# Revit family: VENTS VUTR 281-401 V EC
name_source: partatom
category: Mechanical Equipment
units: mm (PartAtom-declared; Revit-internal decimal feet)

## family parameters
Always vertical = Yes
Cut with Voids When Loaded = No
OmniClass Number = 23.75.00.00
OmniClass Title = Climate Control (HVAC)
Part Type = Normal
Room Calculation Point = No
Round Connector Dimension = Use Diameter
Shared = No
Work Plane-Based = No

## types (8) — shared parameters
00_20_Manufacturer = Vents
00_20_Name = Single-room air handling unit with heat recovery
Casing Material = Polymer-coated steel (white)
D = 160 mm  [stored 0.524934 ft]
Filter = G4
Frequency = 60 Hz
H = 588 mm  [stored 1.92913 ft]
H1 = 638 mm  [stored 2.09318 ft]
L = 515 mm  [stored 1.68963 ft]
L1 = 209 mm  [stored 0.685696 ft]
Load Classification = HVAC
Maintenance zone material = <By Category>
Number of Fase = 1
Voltage = 230 V
W = 598 mm  [stored 1.96194 ft]
W1 = 397 mm  [stored 1.30249 ft]
zero-valued in all types: Default Elevation

## per-type parameters (varying)
| type | Amperage | Maximum Air Flow | Power | Sound pressure level at 3 m distance | Weight |
| VUTR 281 V | 1 A | 382.0 m³/h | 179 W | 26 dBA | 57.00 kg |
| VUTR 401 V | 2 A | 447.0 m³/h | 257 W | 28 dBA | 58.00 kg |
| VUER 281 V | 1 A | 382.0 m³/h | 179 W | 26 dBA | 57.00 kg |
| VUTR 281 VE | 7 A | 382.0 m³/h | 1379 W | 26 dBA | 57.00 kg |
| VUER 281 VE | 7 A | 382.0 m³/h | 1379 W | 26 dBA | 57.00 kg |
| VUER 401 V | 2 A | 447.0 m³/h | 257 W | 28 dBA | 58.00 kg |
| VUTR 401 VE | 7 A | 447.0 m³/h | 1457 W | 28 dBA | 58.00 kg |
| VUER 401 VE | 7 A | 447.0 m³/h | 1457 W | 28 dBA | 58.00 kg |

note: column(s) folded — value = type name in every type: 00_20_Type

note: [stored X ft] marks values corroborated as IEEE doubles in the binary element streams (Revit-internal decimal feet)

## geometry (parser evidence)
native form markers: Sweep x16
no freeform markers — native parametric forms only
